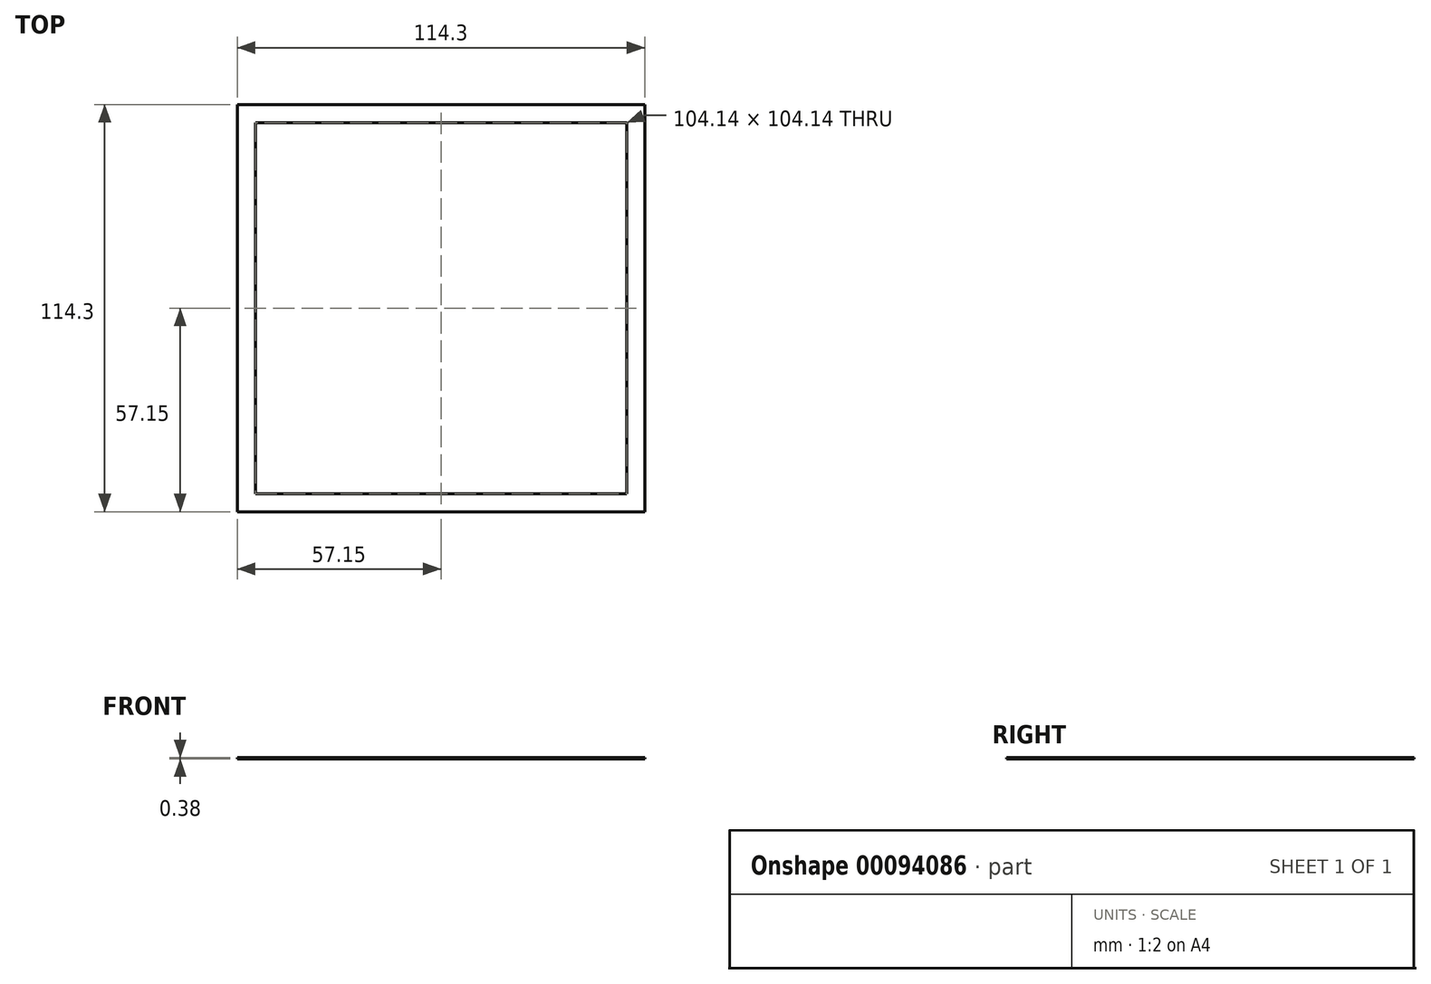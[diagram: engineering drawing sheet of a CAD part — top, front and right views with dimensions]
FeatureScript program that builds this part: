
annotation { "Feature Type Name" : "Feature", "Feature Type Description" : "" }
export const myFeature = defineFeature(function(context is Context, id is Id, definition is map)
    precondition{}
    {
        {
            var Q0;
            Q0=qCreatedBy(makeId("Top.planeOp"),FACE);
            var sketch = newSketch(context, id + "F0", { "sketchPlane" : qUnion([Q0])});
            skLineSegment(sketch, "E0.bottom", {"start": v(0, 0) * mm, "end": v(114.3, 0) * mm});
            skLineSegment(sketch, "E0.top", {"start": v(0, 114.3) * mm, "end": v(114.3, 114.3) * mm});
            skLineSegment(sketch, "E0.left", {"start": v(0, 0) * mm, "end": v(0, 114.3) * mm});
            skLineSegment(sketch, "E0.right", {"start": v(114.3, 0) * mm, "end": v(114.3, 114.3) * mm});
            skLineSegment(sketch, "E1.bottom", {"start": v(5.08, 109.22) * mm, "end": v(109.22, 109.22) * mm});
            skLineSegment(sketch, "E1.top", {"start": v(5.08, 5.08) * mm, "end": v(109.22, 5.08) * mm});
            skLineSegment(sketch, "E1.left", {"start": v(5.08, 109.22) * mm, "end": v(5.08, 5.08) * mm});
            skLineSegment(sketch, "E1.right", {"start": v(109.22, 109.22) * mm, "end": v(109.22, 5.08) * mm});
            skLineSegment(sketch, "E2", {"start": v(57.15, 5.08) * mm, "end": v(57.15, 0) * mm, "construction": true});
            skPoint(sketch, "E2.endSnap0", {"position": v(57.15, 0) * mm});
            skLineSegment(sketch, "E3", {"start": v(109.22, 57.15) * mm, "end": v(114.3, 57.15) * mm, "construction": true});
            skPoint(sketch, "E3.startSnap0", {"position": v(114.3, 57.15) * mm});
            skPoint(sketch, "E3.startSnap1", {"position": v(109.22, 57.15) * mm});
            skSolve(sketch);
        }
        {
            var Q0;
            Q0=makeQuery(id+"F0.imprint","IMPRINT",FACE,{"disambiguationData":[TD([[makeQuery(id+"F0.imprint","IMPRINT",EDGE,{"derivedFrom":sQuery(id+"F0.wireOp",EDGE,"E0.bottom")}),1.0]])]});
            extrude(context, id + "F1", {"entities" : qUnion([Q0]), "depth" : 0.38 * mm, "offsetDistance" : 25.4 * mm});
        }
    });
